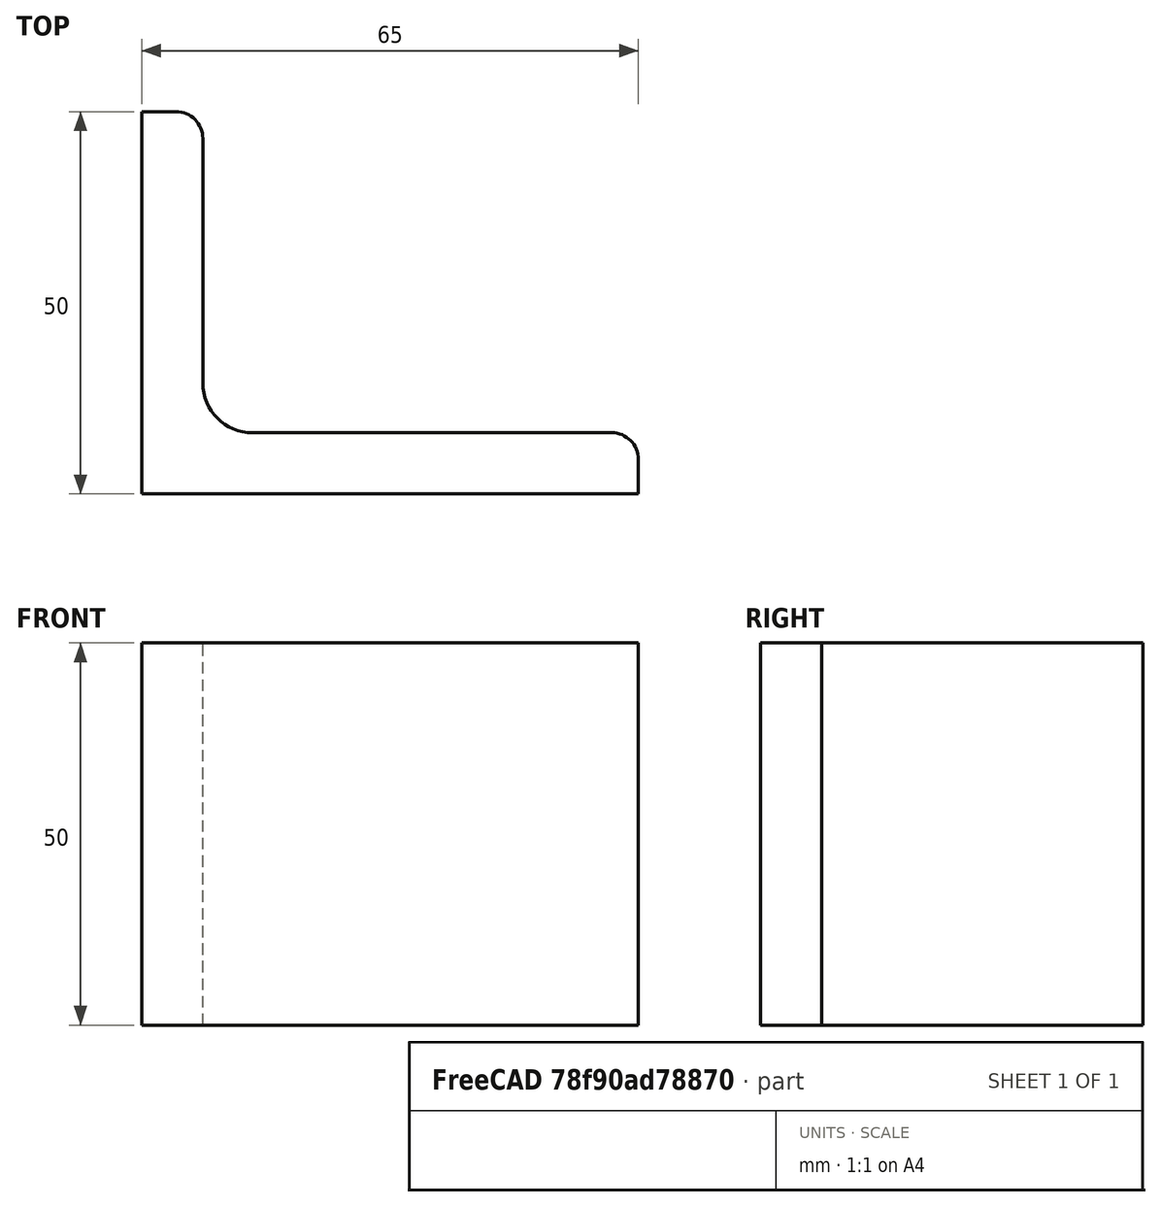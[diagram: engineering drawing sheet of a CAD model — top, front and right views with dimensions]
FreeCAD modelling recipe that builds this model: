
FCSTD DOCUMENT  (FreeCAD 0.15R4671 (Git))
Label: Angle Bar 65x50x8 EN10056 S235JR
License: All rights reserved
LicenseURL: http://en.wikipedia.org/wiki/All_rights_reserved
objects: Sketcher::SketchObject×1, Part::Extrusion×1
note: 2 computed .brp shape members not serialized (recipe doc carries the construction recipe); baked Part::Feature solids carry a one-line shape summary decoded from their .brp

FEATURE [Sketcher::SketchObject] Sketch
  sketch-geometry (9):
    g0: LineSegment StartX=0 StartY=0 StartZ=0 EndX=65 EndY=0 EndZ=0
    g1: LineSegment StartX=65 StartY=0 StartZ=0 EndX=65 EndY=4.5 EndZ=0
    g2: LineSegment StartX=61.5 StartY=8 StartZ=0 EndX=14.5 EndY=8 EndZ=0
    g3: LineSegment StartX=0 StartY=0 StartZ=0 EndX=0 EndY=50 EndZ=0
    g4: LineSegment StartX=0 StartY=50 StartZ=0 EndX=4.5 EndY=50 EndZ=0
    g5: LineSegment StartX=8 StartY=46.5 StartZ=0 EndX=8 EndY=14.5 EndZ=0
    g6: ArcOfCircle CenterX=14.5 CenterY=14.5 CenterZ=0 NormalX=0 NormalY=0 NormalZ=1 Radius=6.5 StartAngle=3.14159 EndAngle=4.71239
    g7: ArcOfCircle CenterX=4.5 CenterY=46.5 CenterZ=0 NormalX=0 NormalY=0 NormalZ=1 Radius=3.5 StartAngle=0 EndAngle=1.5708
    g8: ArcOfCircle CenterX=61.5 CenterY=4.5 CenterZ=0 NormalX=0 NormalY=0 NormalZ=1 Radius=3.5 StartAngle=0 EndAngle=1.5708
  constraints (23):
    c: Coincident(g0,g-1)
    c: Horizontal(g0)
    c: Coincident(g1,g0)
    c: Vertical(g1)
    c: Horizontal(g2)
    c: Coincident(g3,g-1)
    c: Vertical(g3)
    c: Coincident(g4,g3)
    c: Horizontal(g4)
    c: Vertical(g5)
    c: Tangent(g5,g6) = -1.5708
    c: Tangent(g2,g6) = 1.5708
    c: Tangent(g4,g7) = 1.5708
    c: Tangent(g5,g7) = 1.5708
    c: Tangent(g2,g8) = -1.5708
    c: Tangent(g1,g8) = -1.5708
    c: DistanceX(g0) = 65
    c: DistanceY(g3) = 50
    c: DistanceY(g0,g2) = 8
    c: DistanceX(g3,g5) = 8
    c: Radius(g6) = 6.5
    c: Radius(g8) = 3.5
    c: Radius(g7) = 3.5
FEATURE [Part::Extrusion] Extrude  label="Angle Bar 65x50x8 EN10056 S235JR"
  Base = -> Sketch
  Dir = (0,0,50)
  Solid = true
